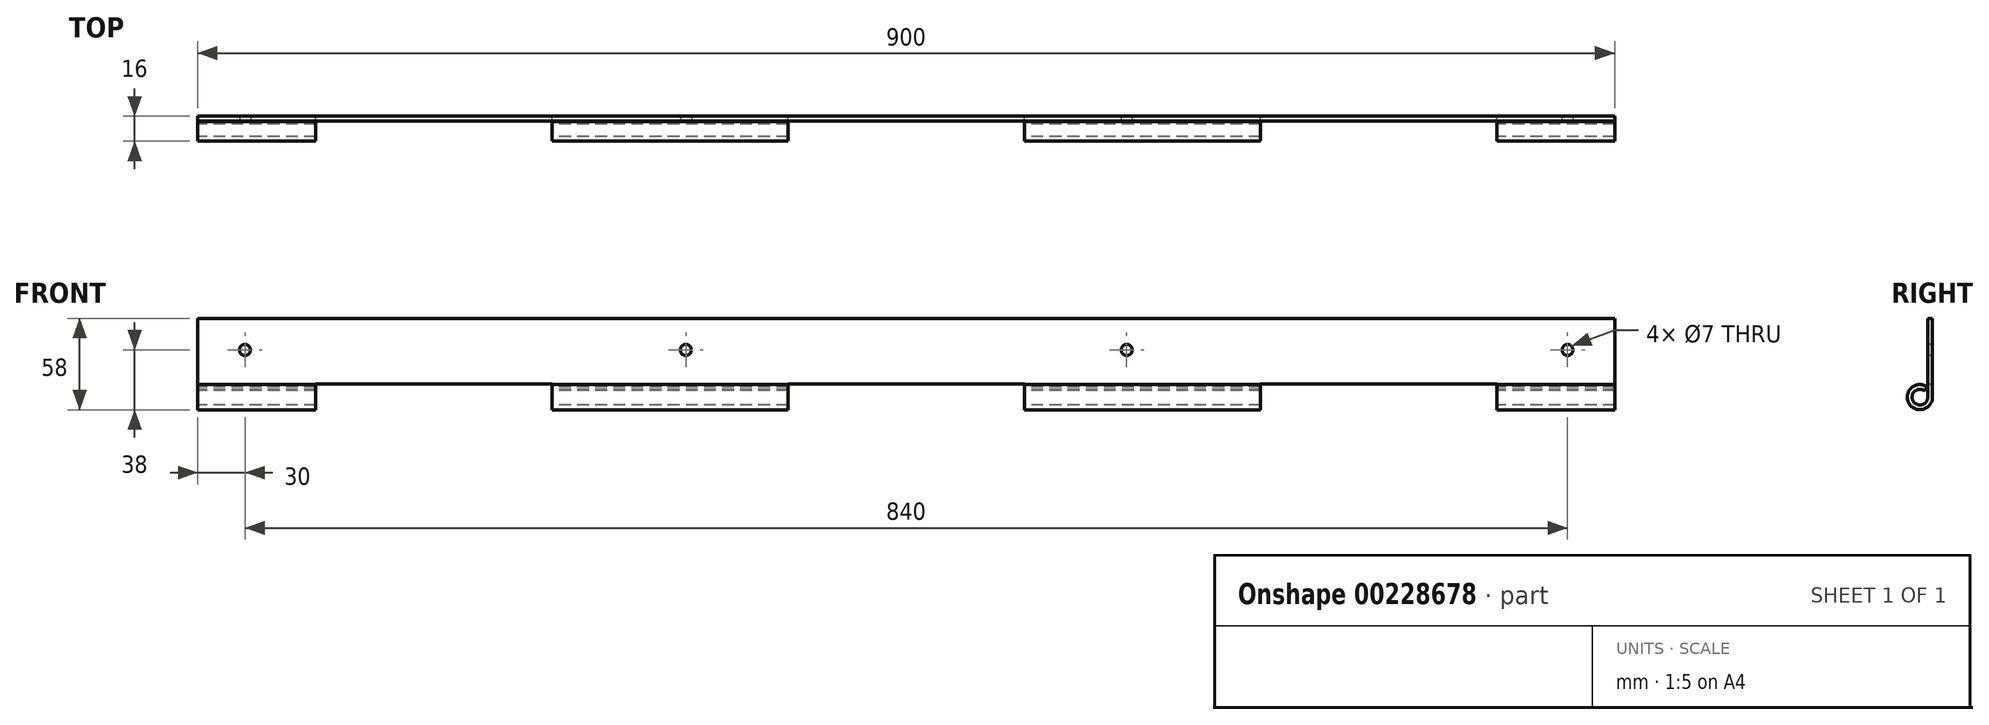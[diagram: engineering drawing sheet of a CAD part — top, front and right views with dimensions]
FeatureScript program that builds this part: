
annotation { "Feature Type Name" : "Feature", "Feature Type Description" : "" }
export const myFeature = defineFeature(function(context is Context, id is Id, definition is map)
    precondition{}
    {
        {
            var Q0;
            Q0=qCreatedBy(makeId("Right.planeOp"),FACE);
            var sketch = newSketch(context, id + "F0", { "sketchPlane" : qUnion([Q0])});
            skArc(sketch, "E0", {"start": v(4.59, 6.55) * mm, "mid": v(-7.1, -3.7) * mm, "end": v(8, 0) * mm});
            skLineSegment(sketch, "E1", {"start": v(8, 0) * mm, "end": v(8, 50) * mm});
            skLineSegment(sketch, "E2", {"start": v(2.87, 4.1) * mm, "end": v(4.59, 6.55) * mm});
            skLineSegment(sketch, "E3.0", {"start": v(5, 0) * mm, "end": v(5, 50) * mm});
            skArc(sketch, "E3.1", {"start": v(2.87, 4.1) * mm, "mid": v(-4.44, -2.3) * mm, "end": v(5, 0) * mm});
            skLineSegment(sketch, "E4", {"start": v(5, 50) * mm, "end": v(8, 50) * mm});
            skSolve(sketch);
        }
        {
            var Q0;
            Q0 = qSketchRegion(id + "F0", true);
            extrude(context, id + "F1", {"entities" : qUnion([Q0]), "endBound" : BoundingType.SYMMETRIC, "depth" : 900 * mm});
        }
        {
            var Q0;
            Q0=qCreatedBy(makeId("Right.planeOp"),FACE);
            cPlane(context, id + "F2", {"entities" : qUnion([Q0]), "cplaneType" : CPlaneType.OFFSET, "offset" : 75 * mm, "oppositeDirection" : true, "width" : 150 * mm, "height" : 150 * mm});
        }
        {
            var Q0;
            Q0=qCreatedBy(id+"F2.planeOp",FACE);
            cPlane(context, id + "F3", {"entities" : qUnion([Q0]), "cplaneType" : CPlaneType.OFFSET, "offset" : 150 * mm, "oppositeDirection" : true, "width" : 150 * mm, "height" : 150 * mm});
        }
        {
            var Q0;
            Q0=qCreatedBy(makeId("Right.planeOp"),FACE);
            cPlane(context, id + "F4", {"entities" : qUnion([Q0]), "cplaneType" : CPlaneType.OFFSET, "offset" : 75 * mm, "width" : 150 * mm, "height" : 150 * mm});
        }
        {
            var Q0;
            Q0=qCreatedBy(id+"F4.planeOp",FACE);
            cPlane(context, id + "F5", {"entities" : qUnion([Q0]), "cplaneType" : CPlaneType.OFFSET, "offset" : 150 * mm, "width" : 150 * mm, "height" : 150 * mm});
        }
        {
            var Q0;
            Q0=qCreatedBy(id+"F5.planeOp",FACE);
            cPlane(context, id + "F6", {"entities" : qUnion([Q0]), "cplaneType" : CPlaneType.OFFSET, "offset" : 150 * mm, "width" : 150 * mm, "height" : 150 * mm});
        }
        {
            var Q0;
            Q0=qCreatedBy(id+"F6.planeOp",FACE);
            cPlane(context, id + "F7", {"entities" : qUnion([Q0]), "cplaneType" : CPlaneType.OFFSET, "offset" : 150 * mm, "width" : 150 * mm, "height" : 150 * mm});
        }
        {
            var Q0;
            Q0=qCreatedBy(id+"F7.planeOp",FACE);
            var sketch = newSketch(context, id + "F8", { "sketchPlane" : qUnion([Q0])});
            skLineSegment(sketch, "E5.bottom", {"start": v(-8.2, 8.2) * mm, "end": v(8.2, 8.2) * mm});
            skLineSegment(sketch, "E5.top", {"start": v(-8.2, -8.2) * mm, "end": v(8.2, -8.2) * mm});
            skLineSegment(sketch, "E5.left", {"start": v(-8.2, 8.2) * mm, "end": v(-8.2, -8.2) * mm});
            skLineSegment(sketch, "E5.right", {"start": v(8.2, 8.2) * mm, "end": v(8.2, -8.2) * mm});
            skSolve(sketch);
        }
        {
            var Q0;
            Q0=qCreatedBy(id+"F6.planeOp",FACE);
            var sketch = newSketch(context, id + "F9", { "sketchPlane" : qUnion([Q0])});
            skLineSegment(sketch, "E6.0", {"start": v(-8.2, 8.2) * mm, "end": v(8.2, 8.2) * mm});
            skLineSegment(sketch, "E6.1", {"start": v(-8.2, -8.2) * mm, "end": v(8.2, -8.2) * mm});
            skLineSegment(sketch, "E6.2", {"start": v(-8.2, 8.2) * mm, "end": v(-8.2, -8.2) * mm});
            skLineSegment(sketch, "E6.3", {"start": v(8.2, 8.2) * mm, "end": v(8.2, -8.2) * mm});
            skSolve(sketch);
        }
        {
            var Q0;
            Q0 = qSketchRegion(id + "F9", true);
            extrude(context, id + "F10", {"entities" : qUnion([Q0]), "operationType" : NewBodyOperationType.REMOVE, "oppositeDirection" : true, "depth" : 150 * mm});
        }
        {
            var Q0;
            Q0=qCreatedBy(id+"F4.planeOp",FACE);
            var sketch = newSketch(context, id + "F11", { "sketchPlane" : qUnion([Q0])});
            skLineSegment(sketch, "E7.0", {"start": v(-8.2, 8.2) * mm, "end": v(8.2, 8.2) * mm});
            skLineSegment(sketch, "E7.1", {"start": v(-8.2, -8.2) * mm, "end": v(8.2, -8.2) * mm});
            skLineSegment(sketch, "E7.2", {"start": v(-8.2, 8.2) * mm, "end": v(-8.2, -8.2) * mm});
            skLineSegment(sketch, "E7.3", {"start": v(8.2, 8.2) * mm, "end": v(8.2, -8.2) * mm});
            skSolve(sketch);
        }
        {
            var Q0;
            Q0 = qSketchRegion(id + "F11", true);
            extrude(context, id + "F12", {"entities" : qUnion([Q0]), "operationType" : NewBodyOperationType.REMOVE, "oppositeDirection" : true, "depth" : 150 * mm});
        }
        {
            var Q0;
            Q0=qCreatedBy(id+"F3.planeOp",FACE);
            var sketch = newSketch(context, id + "F13", { "sketchPlane" : qUnion([Q0])});
            skLineSegment(sketch, "E8.0", {"start": v(-8.2, 8.2) * mm, "end": v(8.2, 8.2) * mm});
            skLineSegment(sketch, "E8.1", {"start": v(-8.2, -8.2) * mm, "end": v(8.2, -8.2) * mm});
            skLineSegment(sketch, "E8.2", {"start": v(-8.2, 8.2) * mm, "end": v(-8.2, -8.2) * mm});
            skLineSegment(sketch, "E8.3", {"start": v(8.2, 8.2) * mm, "end": v(8.2, -8.2) * mm});
            skSolve(sketch);
        }
        {
            var Q0;
            Q0 = qSketchRegion(id + "F13", true);
            extrude(context, id + "F14", {"entities" : qUnion([Q0]), "operationType" : NewBodyOperationType.REMOVE, "oppositeDirection" : true, "depth" : 150 * mm});
        }
        {
            var Q0;
            Q0=qCreatedBy(makeId("Front.planeOp"),FACE);
            var sketch = newSketch(context, id + "F15", { "sketchPlane" : qUnion([Q0])});
            skCircle(sketch, "E9", {"center": v(140, 30) * mm, "radius": 3.5 * mm});
            skCircle(sketch, "E10", {"center": v(-140, 30) * mm, "radius": 3.5 * mm});
            skCircle(sketch, "E11", {"center": v(-420, 30) * mm, "radius": 3.5 * mm});
            skCircle(sketch, "E12", {"center": v(420, 30) * mm, "radius": 3.5 * mm});
            skSolve(sketch);
        }
        {
            var Q0;
            Q0 = qSketchRegion(id + "F15", true);
            extrude(context, id + "F16", {"entities" : qUnion([Q0]), "operationType" : NewBodyOperationType.REMOVE, "endBound" : BoundingType.THROUGH_ALL, "oppositeDirection" : true, "depth" : 25 * mm});
        }
    });
